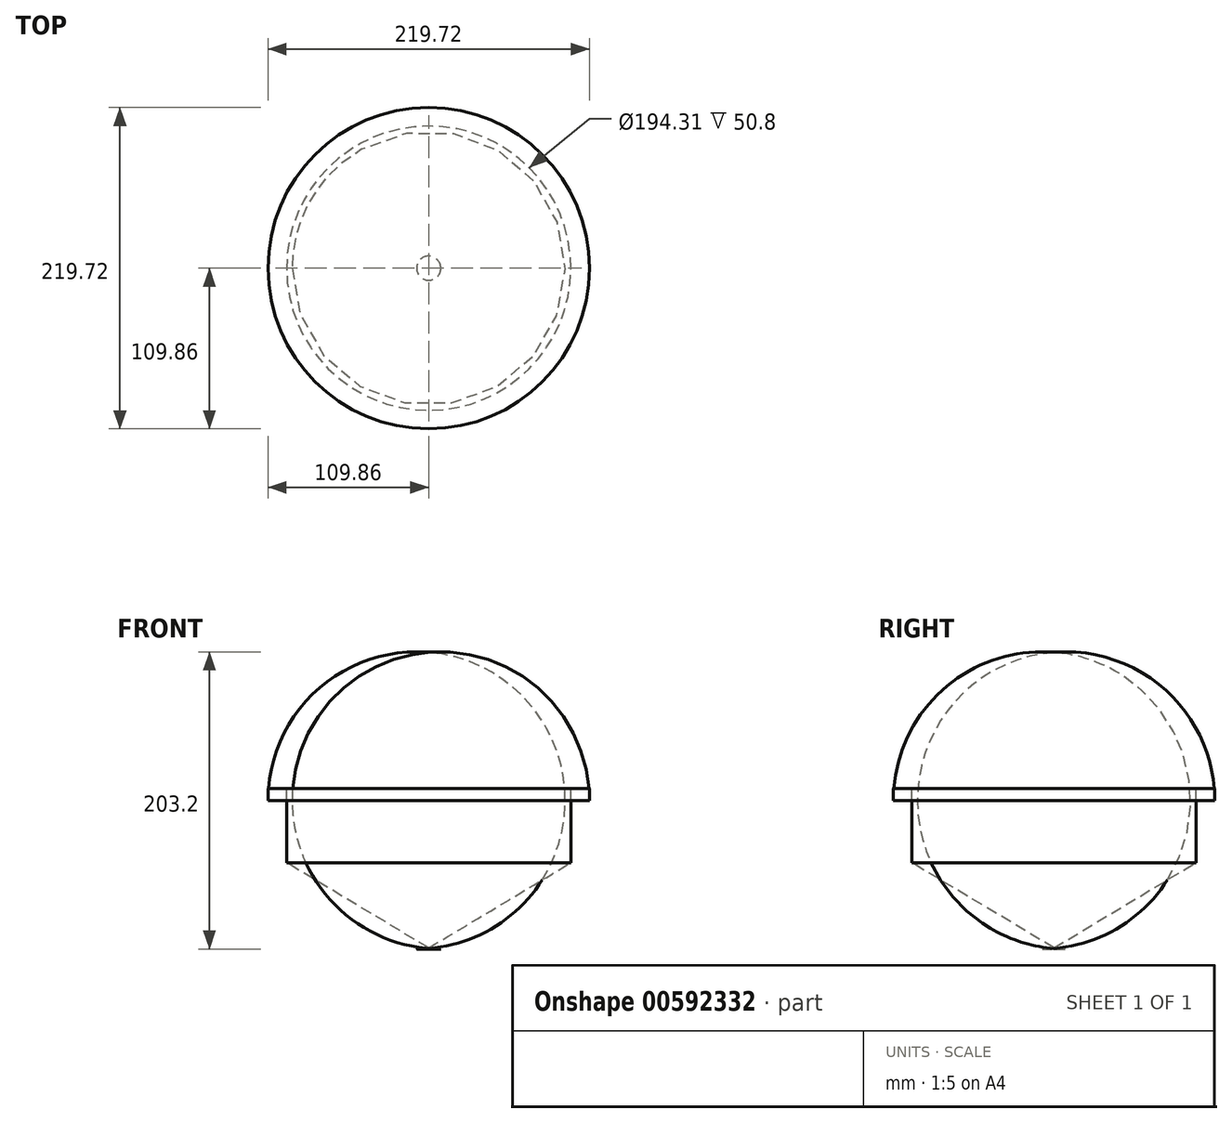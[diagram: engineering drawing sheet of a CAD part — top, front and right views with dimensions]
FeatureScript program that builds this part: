
annotation { "Feature Type Name" : "Feature", "Feature Type Description" : "" }
export const myFeature = defineFeature(function(context is Context, id is Id, definition is map)
    precondition{}
    {
        {
            var Q0;
            Q0=qCreatedBy(makeId("Top.planeOp"),FACE);
            var sketch = newSketch(context, id + "F0", { "sketchPlane" : qUnion([Q0])});
            skCircle(sketch, "E0", {"center": v(0, 0) * mm, "radius": 109.86 * mm});
            skSolve(sketch);
        }
        {
            var Q0;
            Q0=makeQuery(id+"F0.imprint","IMPRINT",FACE,{"disambiguationData":[TD([[makeQuery(id+"F0.imprint","IMPRINT",EDGE,{"derivedFrom":sQuery(id+"F0.wireOp",EDGE,"E0")}),1.0]])]});
            extrude(context, id + "F1", {"entities" : qUnion([Q0]), "depth" : 109.86 * mm, "offsetDistance" : 25.4 * mm});
        }
        {
            var Q0;
            Q0=makeQuery(id+"F1.opExtrude","CAP_FACE",FACE,{"disambiguationData":[OSD([sQuery(id+"F0.wireOp",EDGE,"E0")])],"isStart":false});
            var sketch = newSketch(context, id + "F2", { "sketchPlane" : qUnion([Q0])});
            skCircle(sketch, "E1", {"center": v(0, 0) * mm, "radius": 97.16 * mm});
            skSolve(sketch);
        }
        {
            var Q0;
            Q0=sQuery(id+"F2.wireOp",VERTEX,"E1.center");
            var Q1;
            Q1=makeQuery(id+"F1.opExtrude","SWEPT_BODY",BODY,{"disambiguationData":[OSD([sQuery(id+"F0.wireOp",EDGE,"E0")])]});
            hole(context, id + "F3", {"style" : HoleStyle.SIMPLE, "endStyle" : HoleEndStyle.BLIND, "holeDiameter" : 194.3 * mm, "majorDiameter" : 6.35 * mm, "holeDepth" : 50.8 * mm, "isTappedThrough" : true, "tappedDepth" : 12.7 * mm, "tapClearance" : 3, "locations" : qUnion([Q0]), "scope" : qUnion([Q1])});
        }
        {
            var Q0;
            Q0=makeQuery(id+"F1.opExtrude","CAP_EDGE",EDGE,{"disambiguationData":[OSD([sQuery(id+"F0.wireOp",EDGE,"E0")])],"isStart":true});
            fillet(context, id + "F4", {"entities" : qUnion([Q0]), "radius" : 101.6 * mm, "tangentPropagation" : true, "allowEdgeOverflow" : false});
        }
    });
